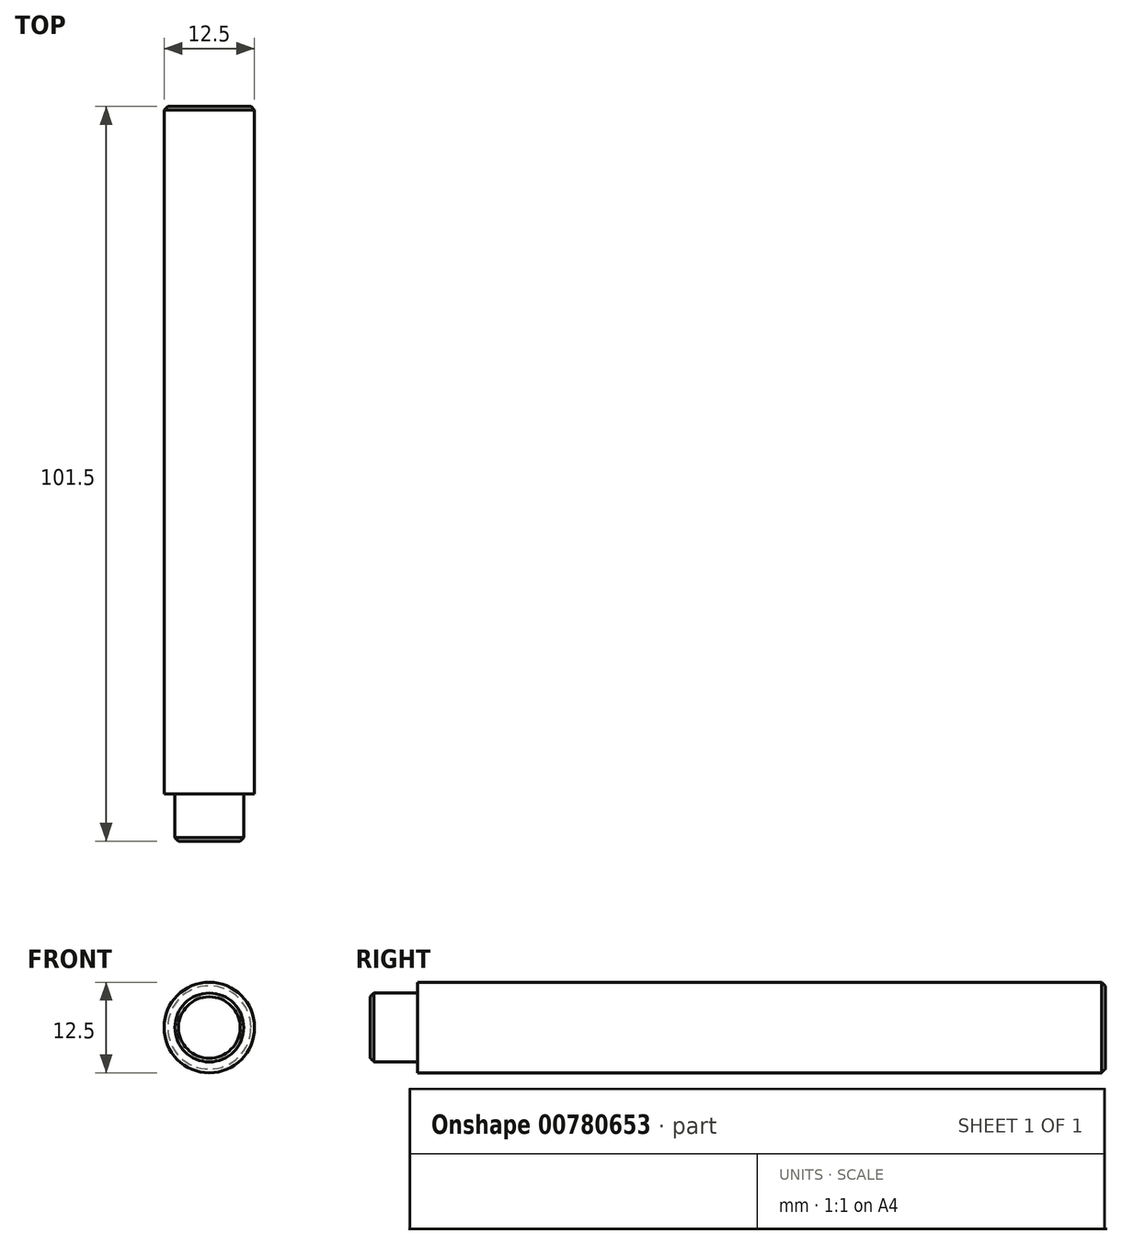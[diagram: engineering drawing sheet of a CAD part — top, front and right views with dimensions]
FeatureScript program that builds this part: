
annotation { "Feature Type Name" : "Feature", "Feature Type Description" : "" }
export const myFeature = defineFeature(function(context is Context, id is Id, definition is map)
    precondition{}
    {
        {
            var Q0;
            Q0=qCreatedBy(makeId("Front.planeOp"),FACE);
            var sketch = newSketch(context, id + "F0", { "sketchPlane" : qUnion([Q0])});
            skCircle(sketch, "E0", {"center": v(0, 0) * mm, "radius": 6.25 * mm});
            skSolve(sketch);
        }
        {
            var Q0;
            Q0 = qSketchRegion(id + "F0", true);
            extrude(context, id + "F1", {"entities" : qUnion([Q0]), "endBound" : BoundingType.SYMMETRIC, "depth" : 95 * mm, "offsetDistance" : 25 * mm});
        }
        {
            var Q0;
            Q0=makeQuery(id+"F1.opExtrude","CAP_FACE",FACE,{"disambiguationData":[OSD([sQuery(id+"F0.wireOp",EDGE,"E0")])],"isStart":false});
            var sketch = newSketch(context, id + "F2", { "sketchPlane" : qUnion([Q0])});
            skCircle(sketch, "E1", {"center": v(0, 0) * mm, "radius": 4.75 * mm});
            skSolve(sketch);
        }
        {
            var Q0;
            Q0 = qSketchRegion(id + "F2", true);
            extrude(context, id + "F3", {"entities" : qUnion([Q0]), "operationType" : NewBodyOperationType.ADD, "depth" : 6.5 * mm, "offsetDistance" : 25 * mm});
        }
        {
            var Q0;
            Q0=makeQuery(id+"F3.opExtrude","CAP_EDGE",EDGE,{"disambiguationData":[OSD([sQuery(id+"F2.wireOp",EDGE,"E1")])],"isStart":false});
            var Q1;
            Q1=makeQuery(id+"F1.opExtrude","CAP_EDGE",EDGE,{"disambiguationData":[OSD([sQuery(id+"F0.wireOp",EDGE,"E0")])],"isStart":true});
            chamfer(context, id + "F4", {"entities" : qUnion([Q0, Q1]), "width" : 0.5 * mm, "tangentPropagation" : true});
        }
    });
